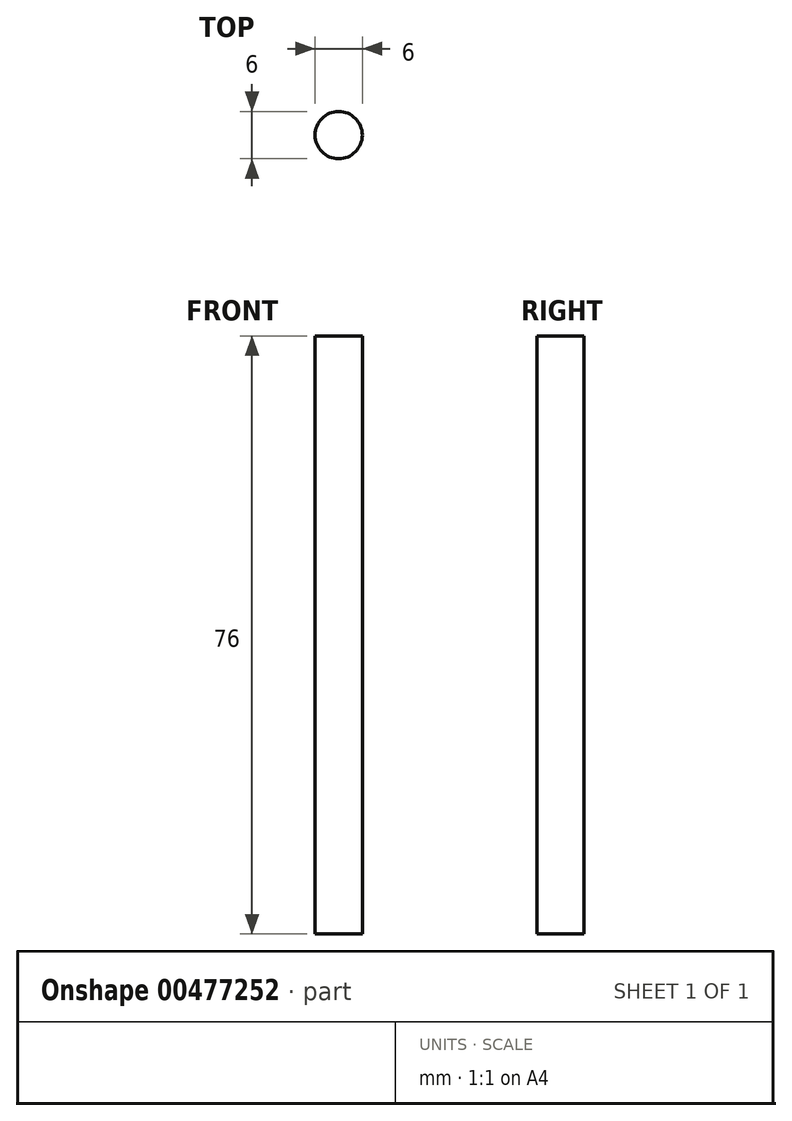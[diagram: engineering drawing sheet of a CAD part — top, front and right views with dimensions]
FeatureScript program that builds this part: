
annotation { "Feature Type Name" : "Feature", "Feature Type Description" : "" }
export const myFeature = defineFeature(function(context is Context, id is Id, definition is map)
    precondition{}
    {
        {
            var Q0;
            Q0=qCreatedBy(makeId("Top.planeOp"),FACE);
            var sketch = newSketch(context, id + "F0", { "sketchPlane" : qUnion([Q0])});
            skCircle(sketch, "E0", {"center": v(0, 0) * mm, "radius": 3 * mm});
            skSolve(sketch);
        }
        {
            var Q0;
            Q0=makeQuery(id+"F0.imprint","IMPRINT",FACE,{"disambiguationData":[TD([[makeQuery(id+"F0.imprint","IMPRINT",EDGE,{"derivedFrom":sQuery(id+"F0.wireOp",EDGE,"E0")}),1.0]])]});
            extrude(context, id + "F1", {"entities" : qUnion([Q0]), "depth" : 76 * mm});
        }
    });
